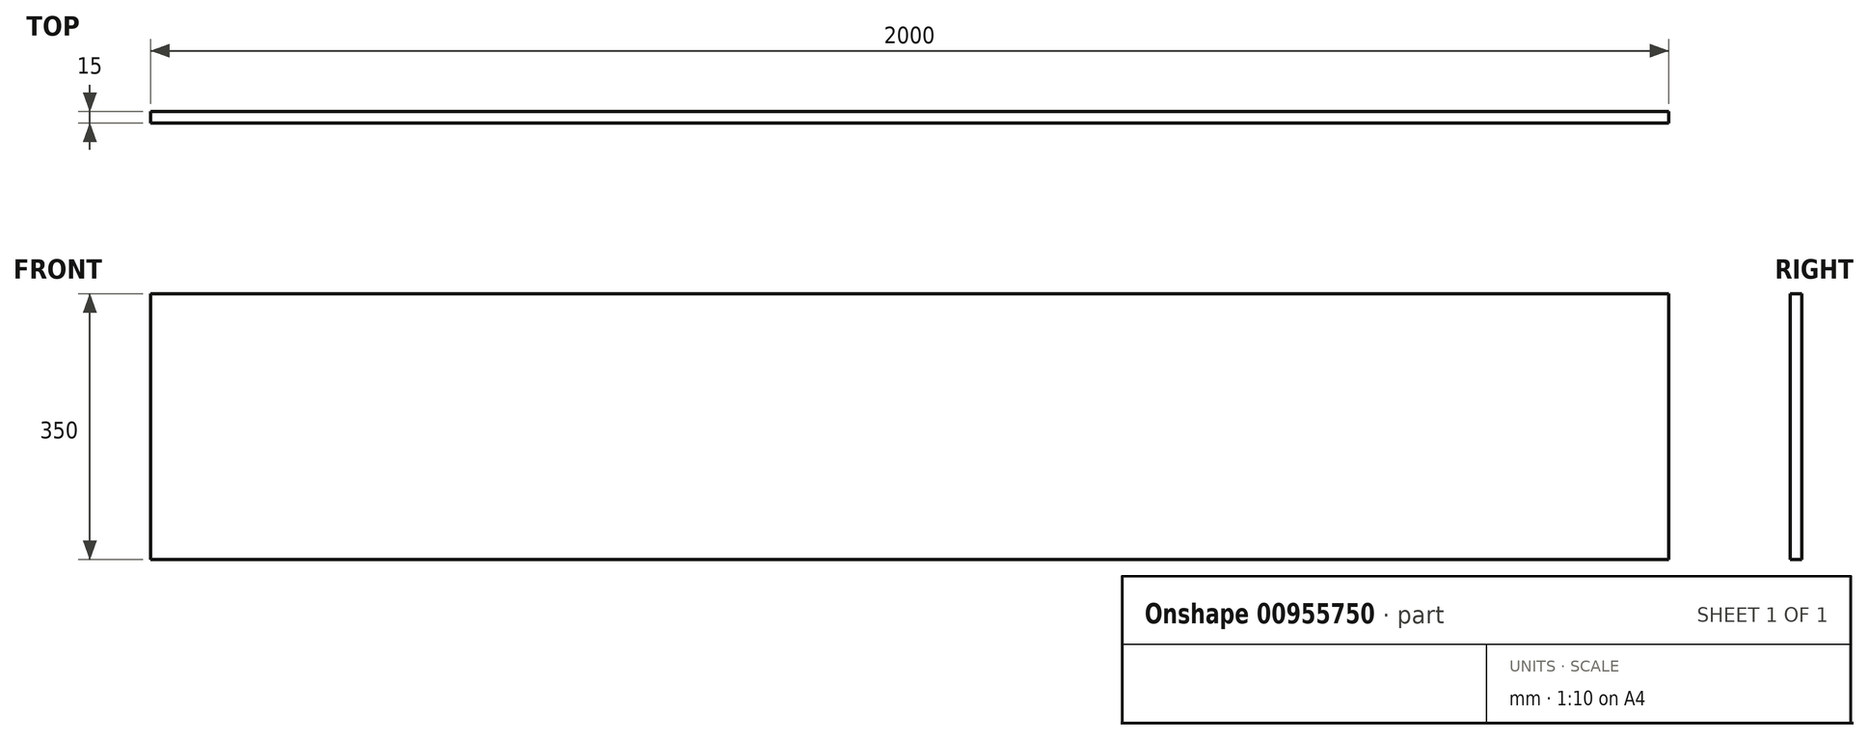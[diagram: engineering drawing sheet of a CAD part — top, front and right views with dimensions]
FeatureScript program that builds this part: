
annotation { "Feature Type Name" : "Feature", "Feature Type Description" : "" }
export const myFeature = defineFeature(function(context is Context, id is Id, definition is map)
    precondition{}
    {
        {
            var Q0;
            Q0=qCreatedBy(makeId("Front.planeOp"),FACE);
            var sketch = newSketch(context, id + "F0", { "sketchPlane" : qUnion([Q0])});
            skLineSegment(sketch, "E0.bottom", {"start": v(0, 0) * mm, "end": v(2000, 0) * mm});
            skLineSegment(sketch, "E0.top", {"start": v(0, -350) * mm, "end": v(2000, -350) * mm});
            skLineSegment(sketch, "E0.left", {"start": v(0, 0) * mm, "end": v(0, -350) * mm});
            skLineSegment(sketch, "E0.right", {"start": v(2000, 0) * mm, "end": v(2000, -350) * mm});
            skSolve(sketch);
        }
        {
            var Q0;
            Q0 = qSketchRegion(id + "F0", true);
            extrude(context, id + "F1", {"entities" : qUnion([Q0]), "depth" : 15 * mm, "offsetDistance" : 25 * mm});
        }
    });
